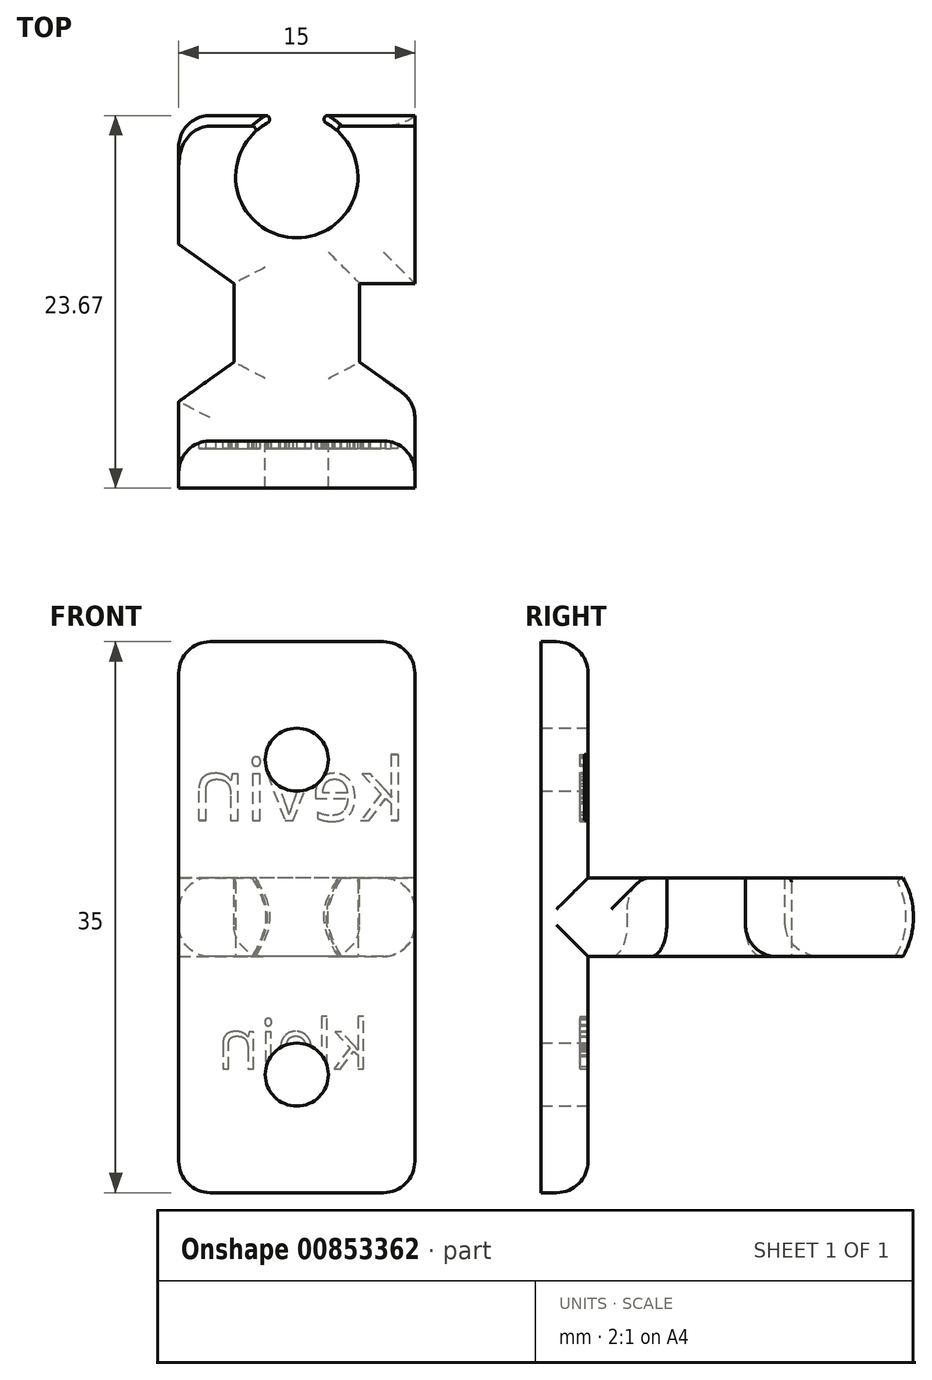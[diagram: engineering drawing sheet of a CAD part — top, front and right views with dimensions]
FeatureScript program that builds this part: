
annotation { "Feature Type Name" : "Feature", "Feature Type Description" : "" }
export const myFeature = defineFeature(function(context is Context, id is Id, definition is map)
    precondition{}
    {
        {
            var Q0;
            Q0=qCreatedBy(makeId("Right.planeOp"),FACE);
            var sketch = newSketch(context, id + "F0", { "sketchPlane" : qUnion([Q0])});
            skLineSegment(sketch, "E0", {"start": v(0, 17.5) * mm, "end": v(0, -17.5) * mm});
            skLineSegment(sketch, "E1", {"start": v(0, -17.5) * mm, "end": v(3, -17.5) * mm});
            skLineSegment(sketch, "E2", {"start": v(3, -17.5) * mm, "end": v(3, -2.5) * mm});
            skLineSegment(sketch, "E3", {"start": v(3, -2.5) * mm, "end": v(23, -2.5) * mm});
            skArc(sketch, "E4", {"start": v(23, -2.5) * mm, "mid": v(23.67, 0) * mm, "end": v(23, 2.5) * mm});
            skLineSegment(sketch, "E5", {"start": v(23, 2.5) * mm, "end": v(3, 2.5) * mm});
            skLineSegment(sketch, "E6", {"start": v(3, 2.5) * mm, "end": v(3, 17.5) * mm});
            skLineSegment(sketch, "E7", {"start": v(3, 17.5) * mm, "end": v(0, 17.5) * mm});
            skSolve(sketch);
        }
        {
            var Q0;
            Q0 = qSketchRegion(id + "F0", true);
            extrude(context, id + "F1", {"entities" : qUnion([Q0]), "depth" : 7.5 * mm, "offsetDistance" : 25 * mm, "hasSecondDirection" : true, "secondDirectionOppositeDirection" : true, "secondDirectionDepth" : 7.5 * mm});
        }
        {
            var Q0;
            Q0=makeQuery(id+"F1.opExtrude","SWEPT_FACE",FACE,{"disambiguationData":[OSD([sQuery(id+"F0.wireOp",EDGE,"E6")])]});
            var sketch = newSketch(context, id + "F2", { "sketchPlane" : qUnion([Q0])});
            skCircle(sketch, "E8", {"center": v(0, 10) * mm, "radius": 2 * mm});
            skSolve(sketch);
        }
        {
            var Q0;
            Q0 = qSketchRegion(id + "F2", true);
            extrude(context, id + "F3", {"entities" : qUnion([Q0]), "operationType" : NewBodyOperationType.REMOVE, "oppositeDirection" : true, "depth" : 25 * mm, "offsetDistance" : 25 * mm});
        }
        {
            var Q0;
            Q0=makeQuery(id+"F1.opExtrude","SWEPT_FACE",FACE,{"disambiguationData":[OSD([sQuery(id+"F0.wireOp",EDGE,"E2")])]});
            var sketch = newSketch(context, id + "F4", { "sketchPlane" : qUnion([Q0])});
            skCircle(sketch, "E9", {"center": v(0, -10) * mm, "radius": 2 * mm});
            skSolve(sketch);
        }
        {
            var Q0;
            Q0 = qSketchRegion(id + "F4", true);
            extrude(context, id + "F5", {"entities" : qUnion([Q0]), "operationType" : NewBodyOperationType.REMOVE, "oppositeDirection" : true, "depth" : 25 * mm, "offsetDistance" : 25 * mm});
        }
        {
            var Q0;
            Q0=makeQuery(id+"F1.opExtrude","SWEPT_FACE",FACE,{"disambiguationData":[OSD([sQuery(id+"F0.wireOp",EDGE,"E5")])]});
            var sketch = newSketch(context, id + "F6", { "sketchPlane" : qUnion([Q0])});
            skLineSegment(sketch, "E10", {"start": v(-7.5, 15.5) * mm, "end": v(-4, 13) * mm});
            skLineSegment(sketch, "E11", {"start": v(-4, 13) * mm, "end": v(-4, 8) * mm});
            skLineSegment(sketch, "E12", {"start": v(-4, 8) * mm, "end": v(-7.5, 5.5) * mm});
            skLineSegment(sketch, "E13", {"start": v(-7.5, 5.5) * mm, "end": v(-7.5, 15.5) * mm});
            skLineSegment(sketch, "E14", {"start": v(7.5, 5.5) * mm, "end": v(4, 8) * mm});
            skLineSegment(sketch, "E15", {"start": v(4, 8) * mm, "end": v(4, 13) * mm});
            skLineSegment(sketch, "E16", {"start": v(4, 13) * mm, "end": v(7.5, 13) * mm});
            skLineSegment(sketch, "E17", {"start": v(7.5, 13) * mm, "end": v(7.5, 5.5) * mm});
            skSolve(sketch);
        }
        {
            var Q0;
            Q0 = qSketchRegion(id + "F6", true);
            extrude(context, id + "F7", {"entities" : qUnion([Q0]), "operationType" : NewBodyOperationType.REMOVE, "oppositeDirection" : true, "depth" : 25 * mm, "offsetDistance" : 25 * mm});
        }
        {
            var Q0;
            Q0=makeQuery(id+"F1.opExtrude","SWEPT_FACE",FACE,{"disambiguationData":[OSD([sQuery(id+"F0.wireOp",EDGE,"E3")])]});
            var sketch = newSketch(context, id + "F8", { "sketchPlane" : qUnion([Q0])});
            skSolve(sketch);
        }
        {
            var Q0;
            {var subQ4=sQuery(id+"F0.wireOp",EDGE,"E3");var subQ5=sQuery(id+"F0.wireOp",EDGE,"E2");Q0=makeQuery(id+"F8.imprint","IMPRINT",FACE,{"disambiguationData":[TD([[makeQuery(id+"F8.imprint","IMPRINT",EDGE,{"derivedFrom":makeQuery(id+"F1.opExtrude","SWEPT_EDGE",EDGE,{"disambiguationData":[OSD([subQ5,subQ4])]})}),1.0]])]});}
            var sketch = newSketch(context, id + "F9", { "sketchPlane" : qUnion([Q0])});
            skCircle(sketch, "E18", {"center": v(0, -19.8) * mm, "radius": 3.88 * mm});
            skSolve(sketch);
        }
        {
            var Q0;
            Q0 = qSketchRegion(id + "F9", true);
            extrude(context, id + "F10", {"entities" : qUnion([Q0]), "operationType" : NewBodyOperationType.REMOVE, "oppositeDirection" : true, "depth" : 25 * mm, "offsetDistance" : 25 * mm});
        }
        {
            var Q0;
            Q0=makeQuery(id+"F10.boolean.opBoolean","INTERSECT",EDGE,{"derivedFrom":[makeQuery(id+"F1.opExtrude","SWEPT_FACE",FACE,{"disambiguationData":[OSD([sQuery(id+"F0.wireOp",EDGE,"E5")])]}),makeQuery(id+"F10.opExtrude","SWEPT_FACE",FACE,{"disambiguationData":[OSD([sQuery(id+"F9.wireOp",EDGE,"E18")])]})]});
            var Q1;
            Q1=makeQuery(id+"F10.boolean.opBoolean","INTERSECT",EDGE,{"disambiguationData":[OD(0.0)],"derivedFrom":[makeQuery(id+"F1.opExtrude","SWEPT_FACE",FACE,{"disambiguationData":[OSD([sQuery(id+"F0.wireOp",EDGE,"E4")])]}),makeQuery(id+"F10.opExtrude","SWEPT_FACE",FACE,{"disambiguationData":[OSD([sQuery(id+"F9.wireOp",EDGE,"E18")])]})]});
            var Q2;
            Q2=makeQuery(id+"F10.boolean.opBoolean","COPY",EDGE,{"derivedFrom":makeQuery(id+"F10.opExtrude","CAP_EDGE",EDGE,{"disambiguationData":[OSD([sQuery(id+"F9.wireOp",EDGE,"E18")])],"isStart":true})});
            var Q3;
            Q3=makeQuery(id+"F10.boolean.opBoolean","INTERSECT",EDGE,{"disambiguationData":[OD(1.0)],"derivedFrom":[makeQuery(id+"F1.opExtrude","SWEPT_FACE",FACE,{"disambiguationData":[OSD([sQuery(id+"F0.wireOp",EDGE,"E4")])]}),makeQuery(id+"F10.opExtrude","SWEPT_FACE",FACE,{"disambiguationData":[OSD([sQuery(id+"F9.wireOp",EDGE,"E18")])]})]});
            fillet(context, id + "F11", {"entities" : qUnion([Q0, Q1, Q2, Q3]), "radius" : 0.25 * mm, "tangentPropagation" : true, "allowEdgeOverflow" : false});
        }
        {
            var Q0;
            Q0=makeQuery(id+"F1.opExtrude","CAP_EDGE",EDGE,{"disambiguationData":[OSD([sQuery(id+"F0.wireOp",EDGE,"E2")])],"isStart":false});
            var Q1;
            Q1=makeQuery(id+"F1.opExtrude","CAP_EDGE",EDGE,{"disambiguationData":[OSD([sQuery(id+"F0.wireOp",EDGE,"E6")])],"isStart":false});
            var Q2;
            Q2=makeQuery(id+"F7.boolean.opBoolean","COPY",EDGE,{"derivedFrom":makeQuery(id+"F7.opExtrude","SWEPT_EDGE",EDGE,{"disambiguationData":[OSD([sQuery(id+"F0.wireOp",EDGE,"E5"),sQuery(id+"F6.wireOp",EDGE,"E14"),sQuery(id+"F6.wireOp",EDGE,"E17")])]})});
            var Q3;
            {var subQ0=sQuery(id+"F0.wireOp",EDGE,"E6");var subQ1=sQuery(id+"F0.wireOp",EDGE,"E5");Q3=makeQuery(id+"F7.boolean.opBoolean","SPLIT",EDGE,{"disambiguationData":[TD([makeQuery(id+"F1.opExtrude","SWEPT_FACE",FACE,{"disambiguationData":[OSD([subQ0])]})])],"derivedFrom":makeQuery(id+"F1.opExtrude","CAP_EDGE",EDGE,{"disambiguationData":[OSD([subQ1])],"isStart":false})});}
            var Q4;
            {var subQ0=sQuery(id+"F0.wireOp",EDGE,"E3");var subQ1=sQuery(id+"F0.wireOp",EDGE,"E2");Q4=makeQuery(id+"F7.boolean.opBoolean","SPLIT",EDGE,{"disambiguationData":[TD([makeQuery(id+"F1.opExtrude","SWEPT_FACE",FACE,{"disambiguationData":[OSD([subQ1])]})])],"derivedFrom":makeQuery(id+"F1.opExtrude","CAP_EDGE",EDGE,{"disambiguationData":[OSD([subQ0])],"isStart":false})});}
            var Q5;
            Q5=makeQuery(id+"F1.opExtrude","SWEPT_EDGE",EDGE,{"disambiguationData":[OSD([sQuery(id+"F0.wireOp",EDGE,"E1"),sQuery(id+"F0.wireOp",EDGE,"E2")])]});
            var Q6;
            Q6=makeQuery(id+"F1.opExtrude","CAP_EDGE",EDGE,{"disambiguationData":[OSD([sQuery(id+"F0.wireOp",EDGE,"E2")])],"isStart":true});
            var Q7;
            Q7=makeQuery(id+"F1.opExtrude","CAP_EDGE",EDGE,{"disambiguationData":[OSD([sQuery(id+"F0.wireOp",EDGE,"E6")])],"isStart":true});
            var Q8;
            {var subQ0=sQuery(id+"F0.wireOp",EDGE,"E6");var subQ1=sQuery(id+"F0.wireOp",EDGE,"E5");Q8=makeQuery(id+"F7.boolean.opBoolean","SPLIT",EDGE,{"disambiguationData":[TD([makeQuery(id+"F1.opExtrude","SWEPT_FACE",FACE,{"disambiguationData":[OSD([subQ0])]})])],"derivedFrom":makeQuery(id+"F1.opExtrude","CAP_EDGE",EDGE,{"disambiguationData":[OSD([subQ1])],"isStart":true})});}
            var Q9;
            {var subQ0=sQuery(id+"F0.wireOp",EDGE,"E3");var subQ1=sQuery(id+"F0.wireOp",EDGE,"E2");Q9=makeQuery(id+"F7.boolean.opBoolean","SPLIT",EDGE,{"disambiguationData":[TD([makeQuery(id+"F1.opExtrude","SWEPT_FACE",FACE,{"disambiguationData":[OSD([subQ1])]})])],"derivedFrom":makeQuery(id+"F1.opExtrude","CAP_EDGE",EDGE,{"disambiguationData":[OSD([subQ0])],"isStart":true})});}
            var Q10;
            Q10=makeQuery(id+"F1.opExtrude","SWEPT_EDGE",EDGE,{"disambiguationData":[OSD([sQuery(id+"F0.wireOp",EDGE,"E6"),sQuery(id+"F0.wireOp",EDGE,"E7")])]});
            var Q11;
            Q11=makeQuery(id+"F1.opExtrude","CAP_EDGE",EDGE,{"disambiguationData":[OSD([sQuery(id+"F0.wireOp",EDGE,"E7")])],"isStart":true});
            var Q12;
            Q12=makeQuery(id+"F1.opExtrude","CAP_EDGE",EDGE,{"disambiguationData":[OSD([sQuery(id+"F0.wireOp",EDGE,"E7")])],"isStart":false});
            var Q13;
            Q13=makeQuery(id+"F1.opExtrude","CAP_EDGE",EDGE,{"disambiguationData":[OSD([sQuery(id+"F0.wireOp",EDGE,"E1")])],"isStart":false});
            var Q14;
            Q14=makeQuery(id+"F1.opExtrude","CAP_EDGE",EDGE,{"disambiguationData":[OSD([sQuery(id+"F0.wireOp",EDGE,"E1")])],"isStart":true});
            var Q15;
            {var subQ0=sQuery(id+"F0.wireOp",EDGE,"E4");var subQ1=sQuery(id+"F0.wireOp",EDGE,"E3");Q15=makeQuery(id+"F7.boolean.opBoolean","SPLIT",EDGE,{"disambiguationData":[TD([makeQuery(id+"F1.opExtrude","SWEPT_FACE",FACE,{"disambiguationData":[OSD([subQ0])]})])],"derivedFrom":makeQuery(id+"F1.opExtrude","CAP_EDGE",EDGE,{"disambiguationData":[OSD([subQ1])],"isStart":false})});}
            var Q16;
            Q16=makeQuery(id+"F1.opExtrude","CAP_EDGE",EDGE,{"disambiguationData":[OSD([sQuery(id+"F0.wireOp",EDGE,"E4")])],"isStart":true});
            var Q17;
            Q17=makeQuery(id+"F7.boolean.opBoolean","COPY",EDGE,{"derivedFrom":makeQuery(id+"F7.opExtrude","CAP_EDGE",EDGE,{"disambiguationData":[OSD([sQuery(id+"F6.wireOp",EDGE,"E11")])],"isStart":true})});
            var Q18;
            Q18=makeQuery(id+"F7.boolean.opBoolean","INTERSECT",EDGE,{"derivedFrom":[makeQuery(id+"F1.opExtrude","SWEPT_FACE",FACE,{"disambiguationData":[OSD([sQuery(id+"F0.wireOp",EDGE,"E3")])]}),makeQuery(id+"F7.opExtrude","SWEPT_FACE",FACE,{"disambiguationData":[OSD([sQuery(id+"F6.wireOp",EDGE,"E11")])]})]});
            var Q19;
            Q19=makeQuery(id+"F7.boolean.opBoolean","COPY",EDGE,{"derivedFrom":makeQuery(id+"F7.opExtrude","CAP_EDGE",EDGE,{"disambiguationData":[OSD([sQuery(id+"F6.wireOp",EDGE,"E10")])],"isStart":true})});
            var Q20;
            Q20=makeQuery(id+"F7.boolean.opBoolean","INTERSECT",EDGE,{"derivedFrom":[makeQuery(id+"F1.opExtrude","SWEPT_FACE",FACE,{"disambiguationData":[OSD([sQuery(id+"F0.wireOp",EDGE,"E3")])]}),makeQuery(id+"F7.opExtrude","SWEPT_FACE",FACE,{"disambiguationData":[OSD([sQuery(id+"F6.wireOp",EDGE,"E10")])]})]});
            var Q21;
            Q21=makeQuery(id+"F7.boolean.opBoolean","INTERSECT",EDGE,{"derivedFrom":[makeQuery(id+"F1.opExtrude","SWEPT_FACE",FACE,{"disambiguationData":[OSD([sQuery(id+"F0.wireOp",EDGE,"E3")])]}),makeQuery(id+"F7.opExtrude","SWEPT_FACE",FACE,{"disambiguationData":[OSD([sQuery(id+"F6.wireOp",EDGE,"E12")])]})]});
            var Q22;
            Q22=makeQuery(id+"F7.boolean.opBoolean","COPY",EDGE,{"derivedFrom":makeQuery(id+"F7.opExtrude","CAP_EDGE",EDGE,{"disambiguationData":[OSD([sQuery(id+"F6.wireOp",EDGE,"E12")])],"isStart":true})});
            var Q23;
            Q23=makeQuery(id+"F7.boolean.opBoolean","COPY",EDGE,{"derivedFrom":makeQuery(id+"F7.opExtrude","CAP_EDGE",EDGE,{"disambiguationData":[OSD([sQuery(id+"F6.wireOp",EDGE,"E15")])],"isStart":true})});
            var Q24;
            Q24=makeQuery(id+"F7.boolean.opBoolean","COPY",EDGE,{"derivedFrom":makeQuery(id+"F7.opExtrude","CAP_EDGE",EDGE,{"disambiguationData":[OSD([sQuery(id+"F6.wireOp",EDGE,"E14")])],"isStart":true})});
            var Q25;
            Q25=makeQuery(id+"F7.boolean.opBoolean","INTERSECT",EDGE,{"derivedFrom":[makeQuery(id+"F1.opExtrude","SWEPT_FACE",FACE,{"disambiguationData":[OSD([sQuery(id+"F0.wireOp",EDGE,"E3")])]}),makeQuery(id+"F7.opExtrude","SWEPT_FACE",FACE,{"disambiguationData":[OSD([sQuery(id+"F6.wireOp",EDGE,"E15")])]})]});
            var Q26;
            Q26=makeQuery(id+"F7.boolean.opBoolean","INTERSECT",EDGE,{"derivedFrom":[makeQuery(id+"F1.opExtrude","SWEPT_FACE",FACE,{"disambiguationData":[OSD([sQuery(id+"F0.wireOp",EDGE,"E3")])]}),makeQuery(id+"F7.opExtrude","SWEPT_FACE",FACE,{"disambiguationData":[OSD([sQuery(id+"F6.wireOp",EDGE,"E14")])]})]});
            var Q27;
            Q27=makeQuery(id+"F7.boolean.opBoolean","INTERSECT",EDGE,{"derivedFrom":[makeQuery(id+"F1.opExtrude","SWEPT_FACE",FACE,{"disambiguationData":[OSD([sQuery(id+"F0.wireOp",EDGE,"E3")])]}),makeQuery(id+"F7.opExtrude","SWEPT_FACE",FACE,{"disambiguationData":[OSD([sQuery(id+"F6.wireOp",EDGE,"E16")])]})]});
            var Q28;
            Q28=makeQuery(id+"F7.boolean.opBoolean","COPY",EDGE,{"derivedFrom":makeQuery(id+"F7.opExtrude","CAP_EDGE",EDGE,{"disambiguationData":[OSD([sQuery(id+"F6.wireOp",EDGE,"E16")])],"isStart":true})});
            fillet(context, id + "F12", {"entities" : qUnion([Q0, Q1, Q2, Q3, Q4, Q5, Q6, Q7, Q8, Q9, Q10, Q11, Q12, Q13, Q14, Q15, Q16, Q17, Q18, Q19, Q20, Q21, Q22, Q23, Q24, Q25, Q26, Q27, Q28]), "radius" : 2 * mm, "tangentPropagation" : true, "allowEdgeOverflow" : false});
        }
        {
            var Q0;
            Q0=makeQuery(id+"F1.opExtrude","SWEPT_FACE",FACE,{"disambiguationData":[OSD([sQuery(id+"F0.wireOp",EDGE,"E2")])]});
            var sketch = newSketch(context, id + "F13", { "sketchPlane" : qUnion([Q0])});
            skText(sketch, "E19", { "text": "kevin", "fontName": "OpenSans-Regular.ttf"});
            const initialGuessF13  = {"E19": [-0.0069, 0.00613, 1, 0, 0.00398]};
            skSetInitialGuess(sketch, initialGuessF13);
            skSolve(sketch);
        }
        {
            var Q0;
            Q0 = qSketchRegion(id + "F13", true);
            extrude(context, id + "F14", {"entities" : qUnion([Q0]), "operationType" : NewBodyOperationType.REMOVE, "oppositeDirection" : true, "depth" : 0.5 * mm, "offsetDistance" : 25 * mm});
        }
        {
            var Q0;
            Q0=makeQuery(id+"F1.opExtrude","SWEPT_FACE",FACE,{"disambiguationData":[OSD([sQuery(id+"F0.wireOp",EDGE,"E2")])]});
            var sketch = newSketch(context, id + "F15", { "sketchPlane" : qUnion([Q0])});
            skText(sketch, "E20", { "text": "klein", "fontName": "OpenSans-Regular.ttf"});
            const initialGuessF15  = {"E20": [-0.0046, -0.00964, 1, 0, 0.00315]};
            skSetInitialGuess(sketch, initialGuessF15);
            skSolve(sketch);
        }
        {
            var Q0;
            Q0 = qSketchRegion(id + "F15", true);
            extrude(context, id + "F16", {"entities" : qUnion([Q0]), "operationType" : NewBodyOperationType.REMOVE, "oppositeDirection" : true, "depth" : 0.5 * mm, "offsetDistance" : 25 * mm});
        }
    });
